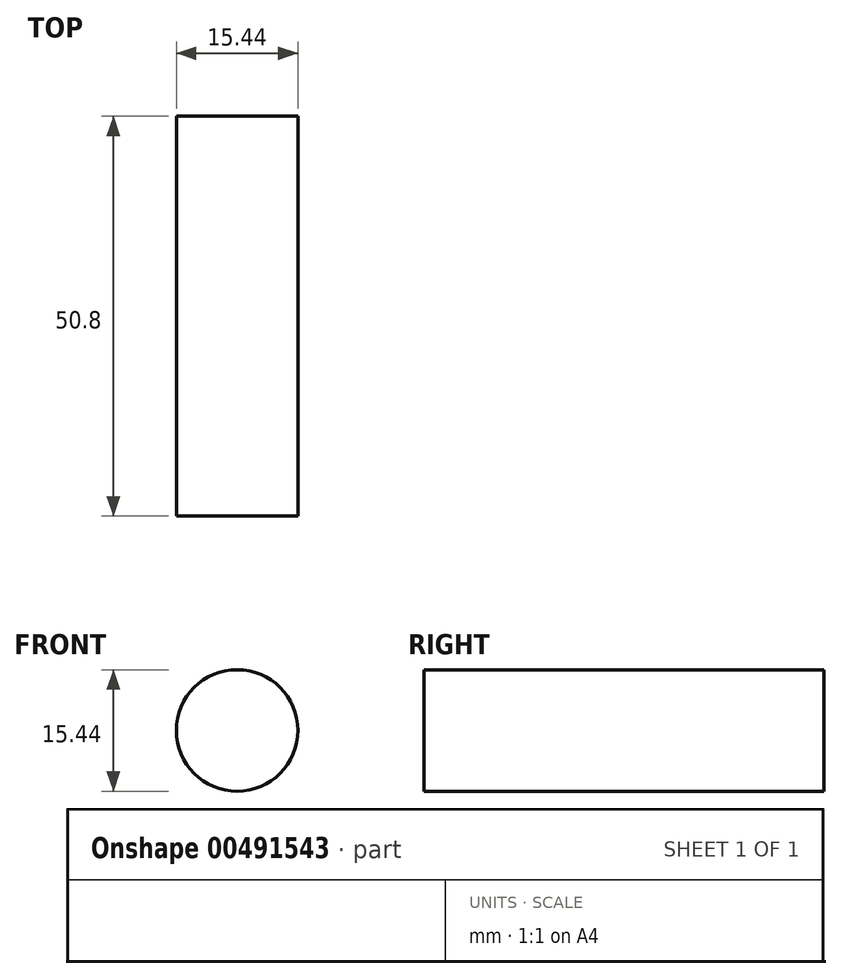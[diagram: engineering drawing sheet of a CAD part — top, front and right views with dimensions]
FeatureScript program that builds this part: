
annotation { "Feature Type Name" : "Feature", "Feature Type Description" : "" }
export const myFeature = defineFeature(function(context is Context, id is Id, definition is map)
    precondition{}
    {
        {
            var Q0;
            Q0=qCreatedBy(makeId("Front.planeOp"),FACE);
            var sketch = newSketch(context, id + "F0", { "sketchPlane" : qUnion([Q0])});
            skCircle(sketch, "E0", {"center": v(-42.1, 0) * mm, "radius": 7.72 * mm});
            skSolve(sketch);
        }
        {
            var Q0;
            Q0 = qSketchRegion(id + "F0", true);
            extrude(context, id + "F1", {"entities" : qUnion([Q0]), "endBound" : BoundingType.SYMMETRIC, "depth" : 50.8 * mm});
        }
    });
